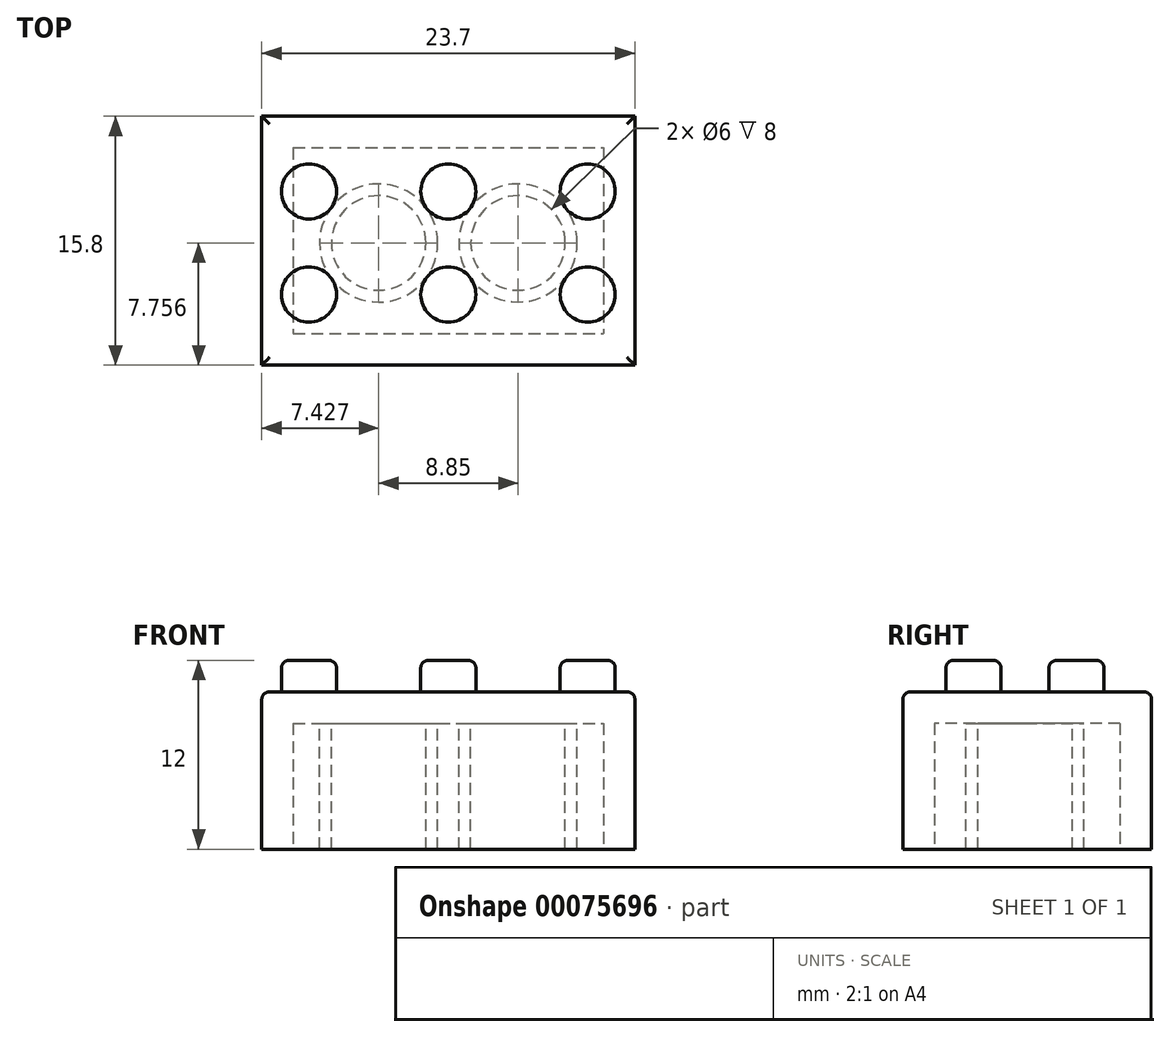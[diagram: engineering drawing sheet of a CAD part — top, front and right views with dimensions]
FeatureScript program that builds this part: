
annotation { "Feature Type Name" : "Feature", "Feature Type Description" : "" }
export const myFeature = defineFeature(function(context is Context, id is Id, definition is map)
    precondition{}
    {
        {
            var Q0;
            Q0=qCreatedBy(makeId("Top.planeOp"),FACE);
            var sketch = newSketch(context, id + "F0", { "sketchPlane" : qUnion([Q0])});
            skLineSegment(sketch, "E0.bottom", {"start": v(-11.32, 1.2) * mm, "end": v(12.38, 1.2) * mm});
            skLineSegment(sketch, "E0.top", {"start": v(-11.32, -14.6) * mm, "end": v(12.38, -14.6) * mm});
            skLineSegment(sketch, "E0.left", {"start": v(-11.32, 1.2) * mm, "end": v(-11.32, -14.6) * mm});
            skLineSegment(sketch, "E0.right", {"start": v(12.38, 1.2) * mm, "end": v(12.38, -14.6) * mm});
            skSolve(sketch);
        }
        {
            var Q0;
            Q0=qCreatedBy(makeId("Top.planeOp"),FACE);
            var sketch = newSketch(context, id + "F1", { "sketchPlane" : qUnion([Q0])});
            skSolve(sketch);
        }
        {
            var Q0;
            Q0 = qSketchRegion(id + "F1", true);
            var Q1;
            Q1=makeQuery(id+"F0.imprint","IMPRINT",FACE,{"disambiguationData":[TD([[makeQuery(id+"F0.imprint","IMPRINT",EDGE,{"derivedFrom":sQuery(id+"F0.wireOp",EDGE,"E0.bottom")}),-1.0]])]});
            extrude(context, id + "F2", {"entities" : qUnion([Q0, Q1]), "depth" : 10 * mm});
        }
        {
            var Q0;
            Q0=makeQuery(id+"F2.opExtrude","CAP_FACE",FACE,{"disambiguationData":[OSD([sQuery(id+"F0.wireOp",EDGE,"E0.bottom"),sQuery(id+"F0.wireOp",EDGE,"E0.top"),sQuery(id+"F0.wireOp",EDGE,"E0.left"),sQuery(id+"F0.wireOp",EDGE,"E0.right")])],"isStart":true});
            var sketch = newSketch(context, id + "F3", { "sketchPlane" : qUnion([Q0])});
            skLineSegment(sketch, "E1.0", {"start": v(10.38, 0.8) * mm, "end": v(10.38, 12.6) * mm});
            skLineSegment(sketch, "E1.1", {"start": v(-9.32, 0.8) * mm, "end": v(10.38, 0.8) * mm});
            skLineSegment(sketch, "E1.2", {"start": v(-9.32, 0.8) * mm, "end": v(-9.32, 12.6) * mm});
            skLineSegment(sketch, "E1.3", {"start": v(-9.32, 12.6) * mm, "end": v(10.38, 12.6) * mm});
            skSolve(sketch);
        }
        {
            var Q0;
            Q0=makeQuery(id+"F3.imprint","IMPRINT",FACE,{"disambiguationData":[TD([[makeQuery(id+"F3.imprint","IMPRINT",EDGE,{"derivedFrom":sQuery(id+"F3.wireOp",EDGE,"E1.0")}),1.0]])]});
            extrude(context, id + "F4", {"entities" : qUnion([Q0]), "operationType" : NewBodyOperationType.REMOVE, "oppositeDirection" : true, "depth" : 8 * mm});
        }
        {
            var Q0;
            Q0=makeQuery(id+"F2.opExtrude","CAP_FACE",FACE,{"disambiguationData":[OSD([sQuery(id+"F0.wireOp",EDGE,"E0.bottom"),sQuery(id+"F0.wireOp",EDGE,"E0.top"),sQuery(id+"F0.wireOp",EDGE,"E0.left"),sQuery(id+"F0.wireOp",EDGE,"E0.right")])],"isStart":false});
            var sketch = newSketch(context, id + "F5", { "sketchPlane" : qUnion([Q0])});
            skLineSegment(sketch, "E2.0", {"start": v(-8.32, -3.57) * mm, "end": v(-8.32, -10.12) * mm, "construction": true});
            skLineSegment(sketch, "E2.1", {"start": v(-8.32, -3.57) * mm, "end": v(9.38, -3.57) * mm, "construction": true});
            skLineSegment(sketch, "E2.3", {"start": v(-8.32, -10.12) * mm, "end": v(9.38, -10.12) * mm, "construction": true});
            skLineSegment(sketch, "E3", {"start": v(0.53, -3.57) * mm, "end": v(0.53, -10.12) * mm, "construction": true});
            skCircle(sketch, "E4", {"center": v(-8.32, -10.12) * mm, "radius": 1.75 * mm});
            skCircle(sketch, "E5", {"center": v(0.53, -10.12) * mm, "radius": 1.75 * mm});
            skCircle(sketch, "E6", {"center": v(9.38, -10.12) * mm, "radius": 1.75 * mm});
            skCircle(sketch, "E7", {"center": v(0.53, -3.57) * mm, "radius": 1.75 * mm});
            skCircle(sketch, "E8", {"center": v(9.38, -3.57) * mm, "radius": 1.75 * mm});
            skCircle(sketch, "E9", {"center": v(-8.32, -3.57) * mm, "radius": 1.75 * mm});
            skSolve(sketch);
        }
        {
            var Q0;
            Q0 = qSketchRegion(id + "F5", true);
            extrude(context, id + "F6", {"entities" : qUnion([Q0]), "operationType" : NewBodyOperationType.ADD, "depth" : 2 * mm});
        }
        {
            var Q0;
            Q0=makeQuery(id+"F4.boolean.opBoolean","COPY",FACE,{"derivedFrom":makeQuery(id+"F4.opExtrude","CAP_FACE",FACE,{"disambiguationData":[OSD([sQuery(id+"F3.wireOp",EDGE,"E1.0"),sQuery(id+"F3.wireOp",EDGE,"E1.1"),sQuery(id+"F3.wireOp",EDGE,"E1.2"),sQuery(id+"F3.wireOp",EDGE,"E1.3")])],"isStart":false})});
            var sketch = newSketch(context, id + "F7", { "sketchPlane" : qUnion([Q0])});
            skCircle(sketch, "E10.0", {"center": v(-8.32, 3.57) * mm, "radius": 1.75 * mm, "construction": true});
            skCircle(sketch, "E11.2", {"center": v(0.53, 10.12) * mm, "radius": 1.75 * mm, "construction": true});
            skLineSegment(sketch, "E12", {"start": v(-8.32, 3.57) * mm, "end": v(0.53, 10.12) * mm, "construction": true});
            skCircle(sketch, "E13.0.0", {"center": v(9.38, 3.57) * mm, "radius": 1.75 * mm});
            skLineSegment(sketch, "E14", {"start": v(0.53, 10.12) * mm, "end": v(9.38, 3.57) * mm, "construction": true});
            skCircle(sketch, "E15", {"center": v(-3.9, 6.84) * mm, "radius": 3.75 * mm});
            skCircle(sketch, "E16", {"center": v(4.96, 6.84) * mm, "radius": 3.75 * mm});
            skCircle(sketch, "E17", {"center": v(-3.9, 6.84) * mm, "radius": 3 * mm});
            skCircle(sketch, "E18", {"center": v(4.96, 6.84) * mm, "radius": 3 * mm});
            skSolve(sketch);
        }
        {
            var Q0;
            Q0=qCreatedBy(makeId("Top.planeOp"),FACE);
            var sketch = newSketch(context, id + "F8", { "sketchPlane" : qUnion([Q0])});
            skSolve(sketch);
        }
        {
            var Q0;
            Q0 = qSketchRegion(id + "F8", true);
            var Q1;
            Q1=makeQuery(id+"F7.imprint","IMPRINT",FACE,{"disambiguationData":[TD([[makeQuery(id+"F7.imprint","IMPRINT",EDGE,{"derivedFrom":sQuery(id+"F7.wireOp",EDGE,"E15")}),1.0]])]});
            var Q2;
            Q2=makeQuery(id+"F7.imprint","IMPRINT",FACE,{"disambiguationData":[TD([[makeQuery(id+"F7.imprint","IMPRINT",EDGE,{"derivedFrom":sQuery(id+"F7.wireOp",EDGE,"E16")}),1.0]])]});
            extrude(context, id + "F9", {"entities" : qUnion([Q0, Q1, Q2]), "operationType" : NewBodyOperationType.ADD, "depth" : 8 * mm});
        }
        {
            var Q0;
            Q0=makeQuery(id+"F6.opExtrude","CAP_EDGE",EDGE,{"disambiguationData":[OSD([sQuery(id+"F5.wireOp",EDGE,"E5")])],"isStart":false});
            var Q1;
            Q1=makeQuery(id+"F6.opExtrude","CAP_EDGE",EDGE,{"disambiguationData":[OSD([sQuery(id+"F5.wireOp",EDGE,"E4")])],"isStart":false});
            var Q2;
            Q2=makeQuery(id+"F6.opExtrude","CAP_EDGE",EDGE,{"disambiguationData":[OSD([sQuery(id+"F5.wireOp",EDGE,"E9")])],"isStart":false});
            var Q3;
            Q3=makeQuery(id+"F6.opExtrude","CAP_EDGE",EDGE,{"disambiguationData":[OSD([sQuery(id+"F5.wireOp",EDGE,"E8")])],"isStart":false});
            var Q4;
            Q4=makeQuery(id+"F6.opExtrude","CAP_EDGE",EDGE,{"disambiguationData":[OSD([sQuery(id+"F5.wireOp",EDGE,"E6")])],"isStart":false});
            var Q5;
            Q5=makeQuery(id+"F6.opExtrude","CAP_EDGE",EDGE,{"disambiguationData":[OSD([sQuery(id+"F5.wireOp",EDGE,"E7")])],"isStart":false});
            fillet(context, id + "F10", {"entities" : qUnion([Q0, Q1, Q2, Q3, Q4, Q5]), "radius" : 0.5 * mm, "tangentPropagation" : true, "allowEdgeOverflow" : false});
        }
        {
            var Q0;
            Q0=makeQuery(id+"F2.opExtrude","CAP_EDGE",EDGE,{"disambiguationData":[OSD([sQuery(id+"F0.wireOp",EDGE,"E0.top")])],"isStart":false});
            var Q1;
            Q1=makeQuery(id+"F2.opExtrude","CAP_EDGE",EDGE,{"disambiguationData":[OSD([sQuery(id+"F0.wireOp",EDGE,"E0.right")])],"isStart":false});
            var Q2;
            Q2=makeQuery(id+"F2.opExtrude","CAP_EDGE",EDGE,{"disambiguationData":[OSD([sQuery(id+"F0.wireOp",EDGE,"E0.bottom")])],"isStart":false});
            var Q3;
            Q3=makeQuery(id+"F2.opExtrude","CAP_EDGE",EDGE,{"disambiguationData":[OSD([sQuery(id+"F0.wireOp",EDGE,"E0.left")])],"isStart":false});
            fillet(context, id + "F11", {"entities" : qUnion([Q0, Q1, Q2, Q3]), "radius" : .5 * mm, "tangentPropagation" : true, "allowEdgeOverflow" : false});
        }
    });
